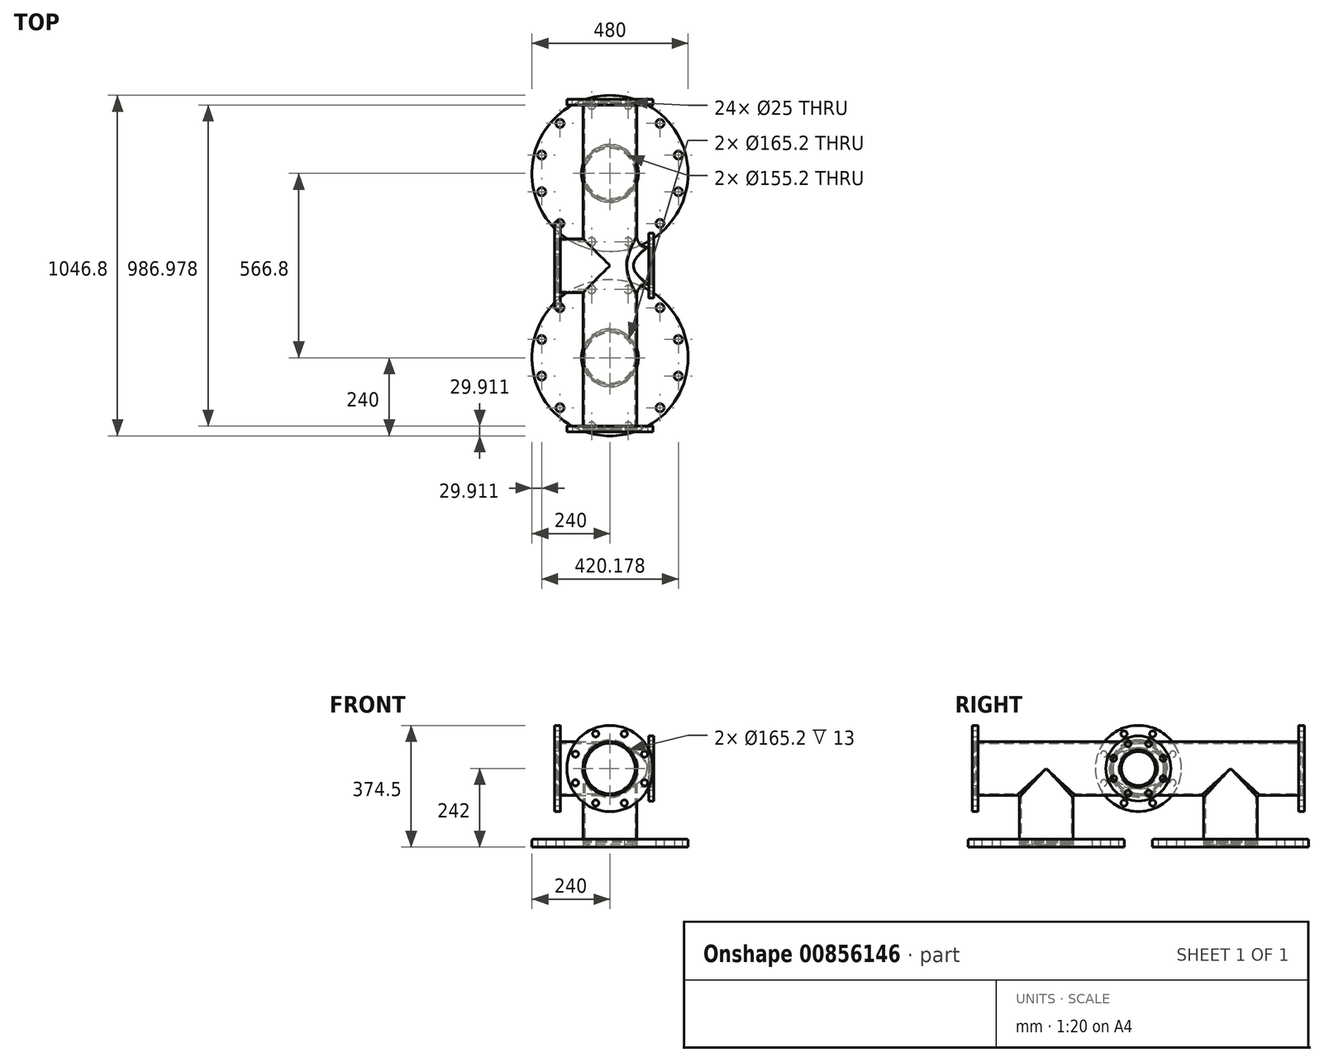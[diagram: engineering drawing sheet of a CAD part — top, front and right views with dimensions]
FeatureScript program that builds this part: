
annotation { "Feature Type Name" : "Feature", "Feature Type Description" : "" }
export const myFeature = defineFeature(function(context is Context, id is Id, definition is map)
    precondition{}
    {
        {
            var Q0;
            Q0=qCreatedBy(makeId("Top.planeOp"),FACE);
            var sketch = newSketch(context, id + "F0", { "sketchPlane" : qUnion([Q0])});
            skCircle(sketch, "E0", {"center": v(0, 0) * mm, "radius": 240 * mm});
            skLineSegment(sketch, "E1", {"start": v(423.48, 0) * mm, "end": v(-426.4, 0) * mm, "construction": true});
            skLineSegment(sketch, "E2", {"start": v(0, 375.02) * mm, "end": v(0, -391.8) * mm, "construction": true});
            skCircle(sketch, "E3", {"center": v(56.3, 210.09) * mm, "radius": 12.5 * mm});
            skCircle(sketch, "E4.1.0", {"center": v(-56.3, 210.09) * mm, "radius": 12.5 * mm});
            skCircle(sketch, "E4.2.0", {"center": v(-153.8, 153.8) * mm, "radius": 12.5 * mm});
            skCircle(sketch, "E4.3.0", {"center": v(-210.09, 56.3) * mm, "radius": 12.5 * mm});
            skCircle(sketch, "E4.4.0", {"center": v(-210.09, -56.3) * mm, "radius": 12.5 * mm});
            skCircle(sketch, "E4.5.0", {"center": v(-153.8, -153.8) * mm, "radius": 12.5 * mm});
            skCircle(sketch, "E4.6.0", {"center": v(-56.3, -210.09) * mm, "radius": 12.5 * mm});
            skCircle(sketch, "E4.7.0", {"center": v(56.3, -210.09) * mm, "radius": 12.5 * mm});
            skCircle(sketch, "E4.8.0", {"center": v(153.8, -153.8) * mm, "radius": 12.5 * mm});
            skCircle(sketch, "E4.9.0", {"center": v(210.09, -56.3) * mm, "radius": 12.5 * mm});
            skCircle(sketch, "E4.10.0", {"center": v(210.09, 56.3) * mm, "radius": 12.5 * mm});
            skCircle(sketch, "E4.11.0", {"center": v(153.8, 153.8) * mm, "radius": 12.5 * mm});
            skCircle(sketch, "E5", {"center": v(0, 0) * mm, "radius": 82.6 * mm});
            skCircle(sketch, "E6", {"center": v(0, 0) * mm, "radius": 217.5 * mm, "construction": true});
            skLineSegment(sketch, "E7", {"start": v(0, 0) * mm, "end": v(-56.3, 210.09) * mm, "construction": true});
            skSolve(sketch);
        }
        {
            var Q0;
            Q0=makeQuery(id+"F0.imprint","IMPRINT",FACE,{"disambiguationData":[TD([[makeQuery(id+"F0.imprint","IMPRINT",EDGE,{"derivedFrom":sQuery(id+"F0.wireOp",EDGE,"E0")}),1.0]])]});
            extrude(context, id + "F1", {"entities" : qUnion([Q0]), "depth" : 24 * mm, "offsetDistance" : 25 * mm});
        }
        {
            var Q0;
            Q0=makeQuery(id+"F1.opExtrude","CAP_EDGE",EDGE,{"disambiguationData":[OSD([sQuery(id+"F0.wireOp",EDGE,"E0")])],"isStart":false});
            fillet(context, id + "F2", {"entities" : qUnion([Q0]), "radius" : 3 * mm, "tangentPropagation" : true, "allowEdgeOverflow" : false});
        }
        {
            var Q0;
            Q0=qCreatedBy(makeId("Top.planeOp"),FACE);
            cPlane(context, id + "F3", {"entities" : qUnion([Q0]), "cplaneType" : CPlaneType.OFFSET, "offset" : 7 * mm, "width" : 150 * mm, "height" : 150 * mm});
        }
        {
            var Q0;
            Q0=qCreatedBy(id+"F3.planeOp",FACE);
            var sketch = newSketch(context, id + "F4", { "sketchPlane" : qUnion([Q0])});
            skCircle(sketch, "E8", {"center": v(0, 0) * mm, "radius": 82.6 * mm});
            skSolve(sketch);
        }
        {
            var Q0;
            Q0 = qSketchRegion(id + "F4", true);
            extrude(context, id + "F5", {"entities" : qUnion([Q0]), "depth" : 235 * mm, "offsetDistance" : 25 * mm});
        }
        {
            var Q0;
            Q0=qCreatedBy(makeId("Right.planeOp"),FACE);
            var sketch = newSketch(context, id + "F6", { "sketchPlane" : qUnion([Q0])});
            skLineSegment(sketch, "E9", {"start": v(321.07, 0) * mm, "end": v(-613.12, 0) * mm, "construction": true});
            skLineSegment(sketch, "E10.0", {"start": v(321.07, 242) * mm, "end": v(-613.12, 242) * mm, "construction": true});
            skLineSegment(sketch, "E11", {"start": v(0, -100.27) * mm, "end": v(0, 349.62) * mm, "construction": true});
            skLineSegment(sketch, "E12.0", {"start": v(-283.4, -100.27) * mm, "end": v(-283.4, 349.62) * mm, "construction": true});
            skCircle(sketch, "E13", {"center": v(-283.4, 242) * mm, "radius": 57.15 * mm});
            skCircle(sketch, "E14", {"center": v(-283.4, 242) * mm, "radius": 82.6 * mm});
            skSolve(sketch);
        }
        {
            var Q0;
            Q0=makeQuery(id+"F6.imprint","IMPRINT",FACE,{"disambiguationData":[TD([[makeQuery(id+"F6.imprint","IMPRINT",EDGE,{"derivedFrom":sQuery(id+"F6.wireOp",EDGE,"E13")}),1.0]])]});
            extrude(context, id + "F7", {"entities" : qUnion([Q0]), "depth" : 130 * mm, "offsetDistance" : 25 * mm});
        }
        {
            var Q0;
            Q0=qCreatedBy(makeId("Front.planeOp"),FACE);
            cPlane(context, id + "F8", {"entities" : qUnion([Q0]), "cplaneType" : CPlaneType.OFFSET, "offset" : 221.6 * mm, "oppositeDirection" : true, "width" : 150 * mm, "height" : 150 * mm});
        }
        {
            var Q0;
            Q0=qCreatedBy(id+"F8.planeOp",FACE);
            var sketch = newSketch(context, id + "F9", { "sketchPlane" : qUnion([Q0])});
            skLineSegment(sketch, "E15", {"start": v(-259.64, 0) * mm, "end": v(218.73, 0) * mm, "construction": true});
            skLineSegment(sketch, "E16", {"start": v(0, -167.32) * mm, "end": v(0, 396.02) * mm, "construction": true});
            skLineSegment(sketch, "E17.0", {"start": v(-259.64, 242) * mm, "end": v(218.73, 242) * mm, "construction": true});
            skCircle(sketch, "E18", {"center": v(0, 242) * mm, "radius": 82.6 * mm});
            skSolve(sketch);
        }
        {
            var Q0;
            Q0=makeQuery(id+"F9.imprint","IMPRINT",FACE,{"disambiguationData":[TD([[makeQuery(id+"F9.imprint","IMPRINT",EDGE,{"derivedFrom":sQuery(id+"F9.wireOp",EDGE,"E18")}),1.0]])]});
            extrude(context, id + "F10", {"entities" : qUnion([Q0]), "depth" : 1010 * mm, "offsetDistance" : 25 * mm});
        }
        {
            var Q0;
            Q0=qCreatedBy(id+"F8.planeOp",FACE);
            cPlane(context, id + "F11", {"entities" : qUnion([Q0]), "cplaneType" : CPlaneType.OFFSET, "offset" : 6 * mm, "oppositeDirection" : true, "width" : 150 * mm, "height" : 150 * mm});
        }
        {
            var Q0;
            Q0=qCreatedBy(id+"F11.planeOp",FACE);
            var sketch = newSketch(context, id + "F12", { "sketchPlane" : qUnion([Q0])});
            skLineSegment(sketch, "E19", {"start": v(0, -86.86) * mm, "end": v(0, 349.16) * mm, "construction": true});
            skLineSegment(sketch, "E20", {"start": v(-135.86, 0) * mm, "end": v(132.36, 0) * mm, "construction": true});
            skLineSegment(sketch, "E21.0", {"start": v(-135.86, 242) * mm, "end": v(132.36, 242) * mm, "construction": true});
            skCircle(sketch, "E22", {"center": v(0, 242) * mm, "radius": 132.5 * mm});
            skCircle(sketch, "E23", {"center": v(0, 242) * mm, "radius": 115 * mm, "construction": true});
            skCircle(sketch, "E24", {"center": v(0, 242) * mm, "radius": 82.6 * mm});
            skLineSegment(sketch, "E25", {"start": v(0, 242) * mm, "end": v(-145.13, 302.12) * mm, "construction": true});
            skCircle(sketch, "E26", {"center": v(-106.25, 286) * mm, "radius": 9.5 * mm});
            skCircle(sketch, "E27.1.0", {"center": v(-106.25, 198) * mm, "radius": 9.5 * mm});
            skCircle(sketch, "E27.2.0", {"center": v(-44, 135.75) * mm, "radius": 9.5 * mm});
            skCircle(sketch, "E27.3.0", {"center": v(44, 135.75) * mm, "radius": 9.5 * mm});
            skCircle(sketch, "E27.4.0", {"center": v(106.25, 198) * mm, "radius": 9.5 * mm});
            skCircle(sketch, "E27.5.0", {"center": v(106.25, 286) * mm, "radius": 9.5 * mm});
            skCircle(sketch, "E27.6.0", {"center": v(44, 348.25) * mm, "radius": 9.5 * mm});
            skCircle(sketch, "E27.7.0", {"center": v(-44, 348.25) * mm, "radius": 9.5 * mm});
            skSolve(sketch);
        }
        {
            var Q0;
            Q0=makeQuery(id+"F12.imprint","IMPRINT",FACE,{"disambiguationData":[TD([[makeQuery(id+"F12.imprint","IMPRINT",EDGE,{"derivedFrom":sQuery(id+"F12.wireOp",EDGE,"E22")}),1.0]])]});
            extrude(context, id + "F13", {"entities" : qUnion([Q0]), "depth" : 18 * mm, "offsetDistance" : 25 * mm});
        }
        {
            var Q0;
            Q0=makeQuery(id+"F13.opExtrude","CAP_EDGE",EDGE,{"disambiguationData":[OSD([sQuery(id+"F12.wireOp",EDGE,"E22")])],"isStart":false});
            fillet(context, id + "F14", {"entities" : qUnion([Q0]), "radius" : 2 * mm, "tangentPropagation" : true, "allowEdgeOverflow" : false});
        }
        {
            var Q0;
            Q0=qCreatedBy(makeId("Front.planeOp"),FACE);
            cPlane(context, id + "F15", {"entities" : qUnion([Q0]), "cplaneType" : CPlaneType.OFFSET, "offset" : 283.4 * mm, "width" : 150 * mm, "height" : 150 * mm});
        }
        {
            var Q0;
            Q0=makeQuery(id+"F1.opExtrude","SWEPT_BODY",BODY,{"disambiguationData":[OSD([sQuery(id+"F0.wireOp",EDGE,"E0"),sQuery(id+"F0.wireOp",EDGE,"E3"),sQuery(id+"F0.wireOp",EDGE,"E4.1.0"),sQuery(id+"F0.wireOp",EDGE,"E4.2.0"),sQuery(id+"F0.wireOp",EDGE,"E4.3.0"),sQuery(id+"F0.wireOp",EDGE,"E4.4.0"),sQuery(id+"F0.wireOp",EDGE,"E4.5.0"),sQuery(id+"F0.wireOp",EDGE,"E4.6.0"),sQuery(id+"F0.wireOp",EDGE,"E4.7.0"),sQuery(id+"F0.wireOp",EDGE,"E4.8.0"),sQuery(id+"F0.wireOp",EDGE,"E4.9.0"),sQuery(id+"F0.wireOp",EDGE,"E4.10.0"),sQuery(id+"F0.wireOp",EDGE,"E4.11.0"),sQuery(id+"F0.wireOp",EDGE,"E4.12.0"),sQuery(id+"F0.wireOp",EDGE,"E4.13.0"),sQuery(id+"F0.wireOp",EDGE,"E4.14.0"),sQuery(id+"F0.wireOp",EDGE,"E4.15.0"),sQuery(id+"F0.wireOp",EDGE,"E4.16.0"),sQuery(id+"F0.wireOp",EDGE,"E4.17.0"),sQuery(id+"F0.wireOp",EDGE,"E4.18.0"),sQuery(id+"F0.wireOp",EDGE,"E4.19.0"),sQuery(id+"F0.wireOp",EDGE,"E5")])]});
            var Q1;
            Q1=makeQuery(id+"F5.opExtrude","SWEPT_BODY",BODY,{"disambiguationData":[OSD([sQuery(id+"F4.wireOp",EDGE,"E8")])]});
            var Q2;
            Q2=makeQuery(id+"F13.opExtrude","SWEPT_BODY",BODY,{"disambiguationData":[OSD([sQuery(id+"F12.wireOp",EDGE,"E22"),sQuery(id+"F12.wireOp",EDGE,"E24"),sQuery(id+"F12.wireOp",EDGE,"E26"),sQuery(id+"F12.wireOp",EDGE,"E27.1.0"),sQuery(id+"F12.wireOp",EDGE,"E27.2.0"),sQuery(id+"F12.wireOp",EDGE,"E27.3.0"),sQuery(id+"F12.wireOp",EDGE,"E27.4.0"),sQuery(id+"F12.wireOp",EDGE,"E27.5.0"),sQuery(id+"F12.wireOp",EDGE,"E27.6.0"),sQuery(id+"F12.wireOp",EDGE,"E27.7.0")])]});
            var Q3;
            Q3=qCreatedBy(id+"F15.planeOp",FACE);
            mirror(context, id + "F16", {"entities" : qUnion([Q0, Q1, Q2]), "mirrorPlane" : qUnion([Q3])});
        }
        {
            var Q0;
            Q0=makeQuery(id+"F6.imprint","IMPRINT",FACE,{"disambiguationData":[TD([[makeQuery(id+"F6.imprint","IMPRINT",EDGE,{"derivedFrom":sQuery(id+"F6.wireOp",EDGE,"E13")}),-1.0]])]});
            var Q1;
            Q1=makeQuery(id+"F6.imprint","IMPRINT",FACE,{"disambiguationData":[TD([[makeQuery(id+"F6.imprint","IMPRINT",EDGE,{"derivedFrom":sQuery(id+"F6.wireOp",EDGE,"E13")}),1.0]])]});
            extrude(context, id + "F17", {"entities" : qUnion([Q0, Q1]), "oppositeDirection" : true, "depth" : 164 * mm, "offsetDistance" : 25 * mm});
        }
        {
            var Q0;
            Q0=makeQuery(id+"F7.opExtrude","SWEPT_BODY",BODY,{"disambiguationData":[OSD([sQuery(id+"F6.wireOp",EDGE,"E13")])]});
            var Q1;
            Q1=makeQuery(id+"F10.opExtrude","SWEPT_BODY",BODY,{"disambiguationData":[OSD([sQuery(id+"F9.wireOp",EDGE,"E18")])]});
            var Q2;
            Q2=makeQuery(id+"F5.opExtrude","SWEPT_BODY",BODY,{"disambiguationData":[OSD([sQuery(id+"F4.wireOp",EDGE,"E8")])]});
            var Q3;
            Q3=makeQuery(id+"F16.opPattern","COPY",BODY,{"derivedFrom":makeQuery(id+"F5.opExtrude","SWEPT_BODY",BODY,{"disambiguationData":[OSD([sQuery(id+"F4.wireOp",EDGE,"E8")])]}),"instanceName":"1"});
            var Q4;
            Q4=makeQuery(id+"F17.opExtrude","SWEPT_BODY",BODY,{"disambiguationData":[OSD([sQuery(id+"F6.wireOp",EDGE,"E14")])]});
            booleanBodies(context, id + "F18", {"operationType" : BooleanOperationType.UNION, "tools" : qUnion([Q0, Q1, Q2, Q3, Q4])});
        }
        {
            var Q0;
            Q0=makeQuery(id+"F18.opBoolean","INTERSECT",EDGE,{"derivedFrom":[makeQuery(id+"F7.opExtrude","SWEPT_FACE",FACE,{"disambiguationData":[OSD([sQuery(id+"F6.wireOp",EDGE,"E13")])]}),makeQuery(id+"F10.opExtrude","SWEPT_FACE",FACE,{"disambiguationData":[OSD([sQuery(id+"F9.wireOp",EDGE,"E18")])]})]});
            fillet(context, id + "F19", {"entities" : qUnion([Q0]), "radius" : 31.73 * mm, "tangentPropagation" : true, "allowEdgeOverflow" : false});
        }
        {
            var Q0;
            Q0=makeQuery(id+"F7.opExtrude","CAP_FACE",FACE,{"disambiguationData":[OSD([sQuery(id+"F6.wireOp",EDGE,"E13")])],"isStart":false});
            var Q1;
            Q1=makeQuery(id+"F10.opExtrude","CAP_FACE",FACE,{"disambiguationData":[OSD([sQuery(id+"F9.wireOp",EDGE,"E18")])],"isStart":false});
            var Q2;
            Q2=makeQuery(id+"F10.opExtrude","CAP_FACE",FACE,{"disambiguationData":[OSD([sQuery(id+"F9.wireOp",EDGE,"E18")])],"isStart":true});
            var Q3;
            Q3=makeQuery(id+"F5.opExtrude","CAP_FACE",FACE,{"disambiguationData":[OSD([sQuery(id+"F4.wireOp",EDGE,"E8")])],"isStart":true});
            var Q4;
            Q4=makeQuery(id+"F16.opPattern","COPY",FACE,{"derivedFrom":makeQuery(id+"F5.opExtrude","CAP_FACE",FACE,{"disambiguationData":[OSD([sQuery(id+"F4.wireOp",EDGE,"E8")])],"isStart":true}),"instanceName":"1"});
            var Q5;
            Q5=makeQuery(id+"F17.opExtrude","CAP_FACE",FACE,{"disambiguationData":[OSD([sQuery(id+"F6.wireOp",EDGE,"E14")])],"isStart":false});
            shell(context, id + "F20", {"entities" : qUnion([Q0, Q1, Q2, Q3, Q4, Q5]), "thickness" : 5 * mm});
        }
        {
            var Q0;
            Q0=makeQuery(id+"F7.opExtrude","CAP_FACE",FACE,{"disambiguationData":[OSD([sQuery(id+"F6.wireOp",EDGE,"E13")])],"isStart":false});
            cPlane(context, id + "F21", {"entities" : qUnion([Q0]), "cplaneType" : CPlaneType.OFFSET, "offset" : 5 * mm, "width" : 150 * mm, "height" : 150 * mm});
        }
        {
            var Q0;
            Q0=qCreatedBy(id+"F21.planeOp",FACE);
            var sketch = newSketch(context, id + "F22", { "sketchPlane" : qUnion([Q0])});
            skLineSegment(sketch, "E28", {"start": v(264.14, 0) * mm, "end": v(-838.48, 0) * mm, "construction": true});
            skLineSegment(sketch, "E29", {"start": v(0, -91.52) * mm, "end": v(0, 421.16) * mm, "construction": true});
            skLineSegment(sketch, "E30.0", {"start": v(-283.4, -91.52) * mm, "end": v(-283.4, 421.16) * mm, "construction": true});
            skLineSegment(sketch, "E31.0", {"start": v(264.14, 242) * mm, "end": v(-838.48, 242) * mm, "construction": true});
            skCircle(sketch, "E32", {"center": v(-283.4, 242) * mm, "radius": 57.15 * mm});
            skCircle(sketch, "E33", {"center": v(-283.4, 242) * mm, "radius": 82.5 * mm, "construction": true});
            skCircle(sketch, "E34", {"center": v(-283.4, 242) * mm, "radius": 100 * mm});
            skLineSegment(sketch, "E35", {"start": v(-283.4, 242) * mm, "end": v(-163.21, 291.78) * mm, "construction": true});
            skCircle(sketch, "E36", {"center": v(-207.18, 273.57) * mm, "radius": 9.5 * mm});
            skCircle(sketch, "E37.1.0", {"center": v(-251.83, 318.22) * mm, "radius": 9.5 * mm});
            skCircle(sketch, "E37.2.0", {"center": v(-314.97, 318.22) * mm, "radius": 9.5 * mm});
            skCircle(sketch, "E37.3.0", {"center": v(-359.62, 273.57) * mm, "radius": 9.5 * mm});
            skCircle(sketch, "E37.4.0", {"center": v(-359.62, 210.43) * mm, "radius": 9.5 * mm});
            skCircle(sketch, "E37.5.0", {"center": v(-314.97, 165.78) * mm, "radius": 9.5 * mm});
            skCircle(sketch, "E37.6.0", {"center": v(-251.83, 165.78) * mm, "radius": 9.5 * mm});
            skCircle(sketch, "E37.7.0", {"center": v(-207.18, 210.43) * mm, "radius": 9.5 * mm});
            skSolve(sketch);
        }
        {
            var Q0;
            Q0=makeQuery(id+"F22.imprint","IMPRINT",FACE,{"disambiguationData":[TD([[makeQuery(id+"F22.imprint","IMPRINT",EDGE,{"derivedFrom":sQuery(id+"F22.wireOp",EDGE,"E32")}),-1.0]])]});
            extrude(context, id + "F23", {"entities" : qUnion([Q0]), "oppositeDirection" : true, "depth" : 16 * mm, "offsetDistance" : 25 * mm});
        }
        {
            var Q0;
            Q0=makeQuery(id+"F23.opExtrude","CAP_EDGE",EDGE,{"disambiguationData":[OSD([sQuery(id+"F22.wireOp",EDGE,"E34")])],"isStart":false});
            fillet(context, id + "F24", {"entities" : qUnion([Q0]), "radius" : 2 * mm, "tangentPropagation" : true, "allowEdgeOverflow" : false});
        }
        {
            var Q0;
            Q0=makeQuery(id+"F17.opExtrude","CAP_FACE",FACE,{"disambiguationData":[OSD([sQuery(id+"F6.wireOp",EDGE,"E14")])],"isStart":false});
            cPlane(context, id + "F25", {"entities" : qUnion([Q0]), "cplaneType" : CPlaneType.OFFSET, "offset" : 6 * mm, "width" : 150 * mm, "height" : 150 * mm});
        }
        {
            var Q0;
            Q0=qCreatedBy(id+"F25.planeOp",FACE);
            var sketch = newSketch(context, id + "F26", { "sketchPlane" : qUnion([Q0])});
            skLineSegment(sketch, "E38", {"start": v(-271.19, 0) * mm, "end": v(825.44, 0) * mm, "construction": true});
            skLineSegment(sketch, "E39", {"start": v(0, -98.6) * mm, "end": v(0, 484.03) * mm, "construction": true});
            skLineSegment(sketch, "E40.0", {"start": v(283.4, -98.6) * mm, "end": v(283.4, 484.03) * mm, "construction": true});
            skLineSegment(sketch, "E41.0", {"start": v(-271.19, 242) * mm, "end": v(825.44, 242) * mm, "construction": true});
            skCircle(sketch, "E42", {"center": v(283.4, 242) * mm, "radius": 132.5 * mm});
            skCircle(sketch, "E43", {"center": v(283.4, 242) * mm, "radius": 115 * mm, "construction": true});
            skCircle(sketch, "E44", {"center": v(283.4, 242) * mm, "radius": 82.6 * mm});
            skLineSegment(sketch, "E45", {"start": v(283.4, 242) * mm, "end": v(138.27, 302.12) * mm, "construction": true});
            skCircle(sketch, "E46", {"center": v(177.15, 286) * mm, "radius": 9.5 * mm});
            skCircle(sketch, "E47.1.0", {"center": v(177.15, 198) * mm, "radius": 9.5 * mm});
            skCircle(sketch, "E47.2.0", {"center": v(239.4, 135.75) * mm, "radius": 9.5 * mm});
            skCircle(sketch, "E47.3.0", {"center": v(327.4, 135.75) * mm, "radius": 9.5 * mm});
            skCircle(sketch, "E47.4.0", {"center": v(389.65, 198) * mm, "radius": 9.5 * mm});
            skCircle(sketch, "E47.5.0", {"center": v(389.65, 286) * mm, "radius": 9.5 * mm});
            skCircle(sketch, "E47.6.0", {"center": v(327.4, 348.25) * mm, "radius": 9.5 * mm});
            skCircle(sketch, "E47.7.0", {"center": v(239.4, 348.25) * mm, "radius": 9.5 * mm});
            skSolve(sketch);
        }
        {
            var Q0;
            Q0=makeQuery(id+"F26.imprint","IMPRINT",FACE,{"disambiguationData":[TD([[makeQuery(id+"F26.imprint","IMPRINT",EDGE,{"derivedFrom":sQuery(id+"F26.wireOp",EDGE,"E42")}),1.0]])]});
            extrude(context, id + "F27", {"entities" : qUnion([Q0]), "oppositeDirection" : true, "depth" : 18 * mm, "offsetDistance" : 25 * mm});
        }
        {
            var Q0;
            Q0=makeQuery(id+"F27.opExtrude","CAP_EDGE",EDGE,{"disambiguationData":[OSD([sQuery(id+"F26.wireOp",EDGE,"E42")])],"isStart":false});
            fillet(context, id + "F28", {"entities" : qUnion([Q0]), "radius" : 2 * mm, "tangentPropagation" : true, "allowEdgeOverflow" : false});
        }
        {
            var Q0;
            Q0=makeQuery(id+"F1.opExtrude","CAP_EDGE",EDGE,{"disambiguationData":[OSD([sQuery(id+"F0.wireOp",EDGE,"E5")])],"isStart":false});
            var Q1;
            Q1=makeQuery(id+"F13.opExtrude","CAP_EDGE",EDGE,{"disambiguationData":[OSD([sQuery(id+"F12.wireOp",EDGE,"E24")])],"isStart":false});
            var Q2;
            Q2=makeQuery(id+"F27.opExtrude","CAP_EDGE",EDGE,{"disambiguationData":[OSD([sQuery(id+"F26.wireOp",EDGE,"E44")])],"isStart":false});
            var Q3;
            Q3=makeQuery(id+"F23.opExtrude","CAP_EDGE",EDGE,{"disambiguationData":[OSD([sQuery(id+"F22.wireOp",EDGE,"E32")])],"isStart":false});
            var Q4;
            Q4=makeQuery(id+"F16.opPattern","COPY",EDGE,{"derivedFrom":makeQuery(id+"F1.opExtrude","CAP_EDGE",EDGE,{"disambiguationData":[OSD([sQuery(id+"F0.wireOp",EDGE,"E5")])],"isStart":false}),"instanceName":"1"});
            var Q5;
            Q5=makeQuery(id+"F16.opPattern","COPY",EDGE,{"derivedFrom":makeQuery(id+"F13.opExtrude","CAP_EDGE",EDGE,{"disambiguationData":[OSD([sQuery(id+"F12.wireOp",EDGE,"E24")])],"isStart":false}),"instanceName":"1"});
            chamfer(context, id + "F29", {"entities" : qUnion([Q0, Q1, Q2, Q3, Q4, Q5]), "width" : 5 * mm, "tangentPropagation" : true});
        }
        {
            var Q0;
            Q0=makeQuery(id+"F7.opExtrude","CAP_EDGE",EDGE,{"disambiguationData":[OSD([sQuery(id+"F6.wireOp",EDGE,"E13")])],"isStart":false});
            chamfer(context, id + "F30", {"entities" : qUnion([Q0]), "width" : 5 * mm, "tangentPropagation" : true});
        }
        {
            var Q0;
            Q0=makeQuery(id+"F17.opExtrude","CAP_EDGE",EDGE,{"disambiguationData":[OSD([sQuery(id+"F6.wireOp",EDGE,"E14")])],"isStart":false});
            chamfer(context, id + "F31", {"entities" : qUnion([Q0]), "chamferType" : ChamferType.TWO_OFFSETS, "width1" : 6 * mm, "oppositeDirection" : false, "width2" : 5.7 * mm, "tangentPropagation" : true});
        }
        {
            var Q0;
            Q0=makeQuery(id+"F16.opPattern","COPY",EDGE,{"derivedFrom":makeQuery(id+"F5.opExtrude","CAP_EDGE",EDGE,{"disambiguationData":[OSD([sQuery(id+"F4.wireOp",EDGE,"E8")])],"isStart":true}),"instanceName":"1"});
            chamfer(context, id + "F32", {"entities" : qUnion([Q0]), "chamferType" : ChamferType.TWO_OFFSETS, "width1" : 5.7 * mm, "oppositeDirection" : false, "width2" : 7 * mm, "tangentPropagation" : true});
        }
        {
            var Q0;
            Q0=makeQuery(id+"F10.opExtrude","CAP_EDGE",EDGE,{"disambiguationData":[OSD([sQuery(id+"F9.wireOp",EDGE,"E18")])],"isStart":true});
            chamfer(context, id + "F33", {"entities" : qUnion([Q0]), "chamferType" : ChamferType.TWO_OFFSETS, "width1" : 6 * mm, "oppositeDirection" : false, "width2" : 5.7 * mm, "tangentPropagation" : true});
        }
        {
            var Q0;
            Q0=makeQuery(id+"F10.opExtrude","CAP_EDGE",EDGE,{"disambiguationData":[OSD([sQuery(id+"F9.wireOp",EDGE,"E18")])],"isStart":false});
            chamfer(context, id + "F34", {"entities" : qUnion([Q0]), "chamferType" : ChamferType.TWO_OFFSETS, "width1" : 5.7 * mm, "oppositeDirection" : false, "width2" : 6 * mm, "tangentPropagation" : true});
        }
        {
            var Q0;
            Q0=makeQuery(id+"F5.opExtrude","CAP_EDGE",EDGE,{"disambiguationData":[OSD([sQuery(id+"F4.wireOp",EDGE,"E8")])],"isStart":true});
            chamfer(context, id + "F35", {"entities" : qUnion([Q0]), "chamferType" : ChamferType.TWO_OFFSETS, "width1" : 7 * mm, "oppositeDirection" : false, "width2" : 5.7 * mm, "tangentPropagation" : true});
        }
        {
            var Q0;
            Q0=makeQuery(id+"F18.opBoolean","INTERSECT",EDGE,{"disambiguationData":[OD(0.0)],"derivedFrom":[makeQuery(id+"F10.opExtrude","SWEPT_FACE",FACE,{"disambiguationData":[OSD([sQuery(id+"F9.wireOp",EDGE,"E18")])]}),makeQuery(id+"F16.opPattern","COPY",FACE,{"derivedFrom":makeQuery(id+"F5.opExtrude","SWEPT_FACE",FACE,{"disambiguationData":[OSD([sQuery(id+"F4.wireOp",EDGE,"E8")])]}),"instanceName":"1"})]});
            var Q1;
            Q1=makeQuery(id+"F18.opBoolean","INTERSECT",EDGE,{"disambiguationData":[OD(1.0)],"derivedFrom":[makeQuery(id+"F10.opExtrude","SWEPT_FACE",FACE,{"disambiguationData":[OSD([sQuery(id+"F9.wireOp",EDGE,"E18")])]}),makeQuery(id+"F16.opPattern","COPY",FACE,{"derivedFrom":makeQuery(id+"F5.opExtrude","SWEPT_FACE",FACE,{"disambiguationData":[OSD([sQuery(id+"F4.wireOp",EDGE,"E8")])]}),"instanceName":"1"})]});
            var Q2;
            Q2=makeQuery(id+"F18.opBoolean","INTERSECT",EDGE,{"disambiguationData":[OD(0.0)],"derivedFrom":[makeQuery(id+"F5.opExtrude","SWEPT_FACE",FACE,{"disambiguationData":[OSD([sQuery(id+"F4.wireOp",EDGE,"E8")])]}),makeQuery(id+"F10.opExtrude","SWEPT_FACE",FACE,{"disambiguationData":[OSD([sQuery(id+"F9.wireOp",EDGE,"E18")])]})]});
            var Q3;
            Q3=makeQuery(id+"F18.opBoolean","INTERSECT",EDGE,{"disambiguationData":[OD(1.0)],"derivedFrom":[makeQuery(id+"F5.opExtrude","SWEPT_FACE",FACE,{"disambiguationData":[OSD([sQuery(id+"F4.wireOp",EDGE,"E8")])]}),makeQuery(id+"F10.opExtrude","SWEPT_FACE",FACE,{"disambiguationData":[OSD([sQuery(id+"F9.wireOp",EDGE,"E18")])]})]});
            fillet(context, id + "F36", {"entities" : qUnion([Q0, Q1, Q2, Q3]), "radius" : 7 * mm, "tangentPropagation" : true, "allowEdgeOverflow" : false});
        }
    });
